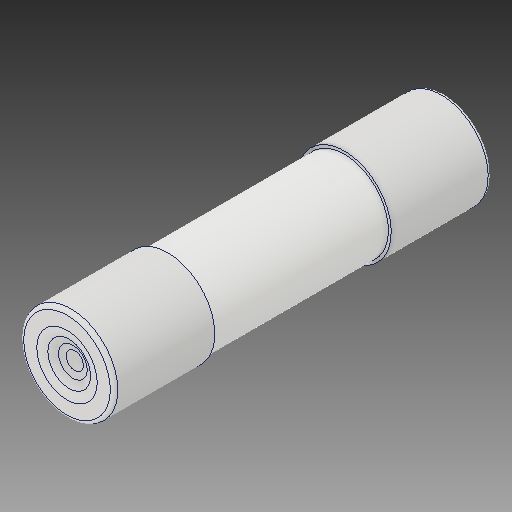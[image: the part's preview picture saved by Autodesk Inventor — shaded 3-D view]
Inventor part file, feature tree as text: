
AUTODESK INVENTOR PART (.ipt)
format: ipt  version: 2019.4 (Build 234330000, 330)  size: 232,448 bytes
history: native  units: mm
features: other x2, revolve x1
ambient origin geometry x8: Origin, YZ Plane, XZ Plane, XY Plane, X Axis, Y Axis, Z Axis, Center Point
bodies: Solid1 (feature_tree), Solid2 (feature_tree), Solid3 (feature_tree)
feature tree (3):
  other  "Boss-Extrude1"
  revolve  "Revolve3[2]"  [1 undecoded]
  other  "Boss-Extrude2"
note: 1 required parameter value undecoded (feature->parameter linkage not recoverable at this tier; creation-order binding heuristic only, values carry confidence <= 0.55)
